# Revit family: Picnic 1800 High
name_source: partatom
category: Furniture
revit_build: Autodesk Revit 2017 (Build: 20171027_0315(x64)
units: mm (PartAtom-declared; Revit-internal decimal feet)

## family parameters
Always vertical = Yes
Cut with Voids When Loaded = No
OmniClass Number = 23.40.20.00
OmniClass Title = General Furniture and Specialties
Room Calculation Point = No
Shared = No
Work Plane-Based = No

## types (1)
- Picnic 1800 High
    Design Year = 2021
    Designer = Form Us With Love
    Diameter (cm) = 180
    EN Strength, durability and safety = EN 15372:2016 - EN 16139:2013 - L2: Extreme use
    Environment = FSC-C163859
    Frame = +Halle Powdercoated steel - RAL 9005
    Gliders = +Halle Plastic - RAL 9005
    Height (cm) = 100
    Packaging Dimensions (cm) = 180 / 80 / 240
    Product family = Picnic
    Seat = +Halle Mood 2106
    Seating Height (cm) = 79
    Table Diameter (cm) = 96
    Table top = +Halle Oak Solid Horizontal
    URL = https://www.plushalle.com
    Warranty period = 2 years standard warranty
    Weight (kg) = 137

## geometry (parser evidence)
native form markers: Sweep x2
no freeform markers — native parametric forms only
